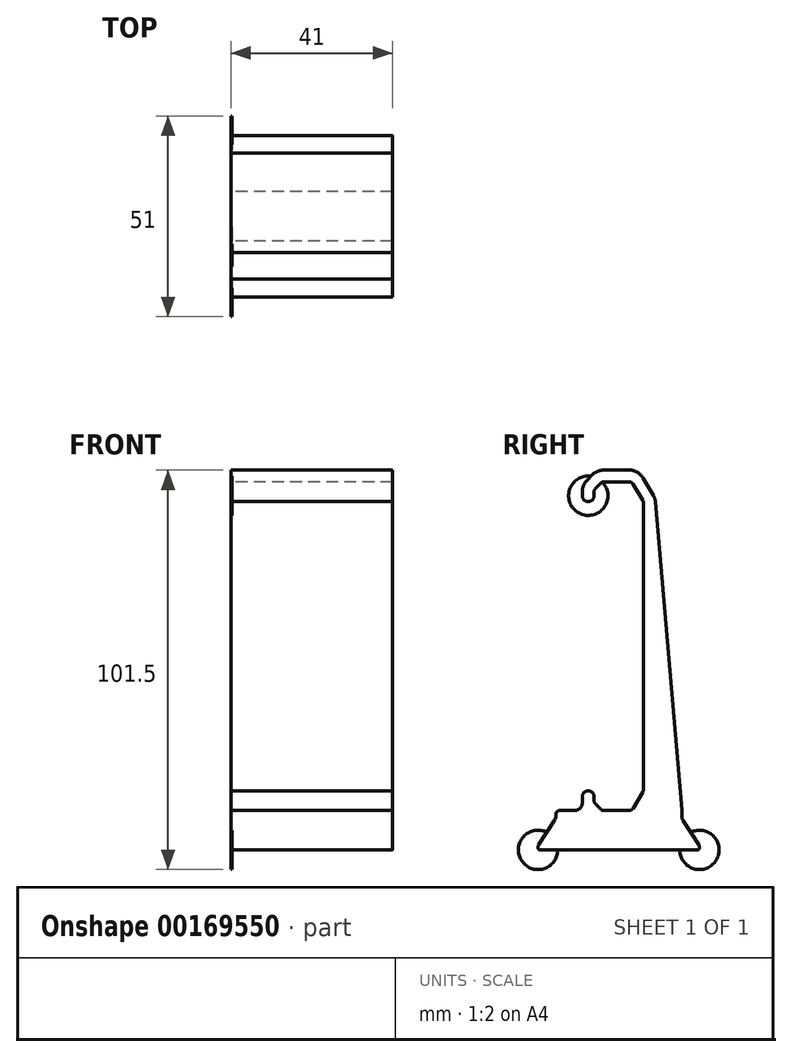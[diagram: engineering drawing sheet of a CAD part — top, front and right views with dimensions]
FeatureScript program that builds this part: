
annotation { "Feature Type Name" : "Feature", "Feature Type Description" : "" }
export const myFeature = defineFeature(function(context is Context, id is Id, definition is map)
    precondition{}
    {
        {
            var Q0;
            Q0=qCreatedBy(makeId("Right.planeOp"),FACE);
            var sketch = newSketch(context, id + "F0", { "sketchPlane" : qUnion([Q0])});
            skLineSegment(sketch, "E0", {"start": v(0, 0) * mm, "end": v(-20, 0) * mm});
            skLineSegment(sketch, "E1", {"start": v(-20.5, 0.5) * mm, "end": v(-20.5, 0.7) * mm});
            skLineSegment(sketch, "E2", {"start": v(-16, 8) * mm, "end": v(0, 8) * mm, "construction": true});
            skLineSegment(sketch, "E3", {"start": v(0, 8) * mm, "end": v(0, 0) * mm, "construction": true});
            skLineSegment(sketch, "E4", {"start": v(-16, 8.59) * mm, "end": v(-16, 9) * mm});
            skLineSegment(sketch, "E5", {"start": v(-3.84, 10) * mm, "end": v(0, 10) * mm});
            skLineSegment(sketch, "E6", {"start": v(0, 10) * mm, "end": v(0, 8) * mm, "construction": true});
            skLineSegment(sketch, "E7", {"start": v(-20.34, 1.25) * mm, "end": v(-16.32, 7.5) * mm});
            skLineSegment(sketch, "E8.MirrorCS", {"start": v(2.68, 10) * mm, "end": v(0, 10) * mm});
            skLineSegment(sketch, "E9.MirrorCS", {"start": v(16, 8.59) * mm, "end": v(16, 9.98) * mm});
            skLineSegment(sketch, "E10.MirrorCS", {"start": v(16, 8) * mm, "end": v(0, 8) * mm, "construction": true});
            skLineSegment(sketch, "E11.MirrorCS", {"start": v(20.34, 1.25) * mm, "end": v(16.32, 7.5) * mm});
            skLineSegment(sketch, "E12.MirrorCS", {"start": v(20.5, 0.5) * mm, "end": v(20.5, 0.7) * mm});
            skLineSegment(sketch, "E13.MirrorCS", {"start": v(0, 0) * mm, "end": v(20, 0) * mm});
            skLineSegment(sketch, "E14", {"start": v(6.25, 15.28) * mm, "end": v(6.25, 88.22) * mm});
            skLineSegment(sketch, "E15", {"start": v(2.68, 93.5) * mm, "end": v(-3.84, 93.5) * mm});
            skLineSegment(sketch, "E16", {"start": v(-6.25, 91.09) * mm, "end": v(-6.25, 90) * mm});
            skLineSegment(sketch, "E17", {"start": v(3.54, 10.49) * mm, "end": v(6.1, 14.76) * mm});
            skLineSegment(sketch, "E18", {"start": v(-4.54, 10.3) * mm, "end": v(-5.96, 11.7) * mm});
            skLineSegment(sketch, "E19", {"start": v(-4.54, 93.2) * mm, "end": v(-5.96, 91.8) * mm});
            skLineSegment(sketch, "E20", {"start": v(3.54, 93.01) * mm, "end": v(6.1, 88.74) * mm});
            skPoint(sketch, "E21.orphan", {"position": v(-6.25, 93.5) * mm});
            skPoint(sketch, "E22.orphan", {"position": v(6.25, 93.5) * mm});
            skPoint(sketch, "E23.orphan", {"position": v(-6.25, 10) * mm});
            skPoint(sketch, "E24.orphan", {"position": v(6.25, 10) * mm});
            skLineSegment(sketch, "E25", {"start": v(-6.25, 10) * mm, "end": v(-6.25, 12) * mm, "construction": true});
            skLineSegment(sketch, "E26", {"start": v(6.25, 10) * mm, "end": v(6.25, 15) * mm, "construction": true});
            skLineSegment(sketch, "E27", {"start": v(-6.25, 93.5) * mm, "end": v(-4.25, 93.5) * mm, "construction": true});
            skLineSegment(sketch, "E28", {"start": v(-6.25, 93.5) * mm, "end": v(-6.25, 91.5) * mm, "construction": true});
            skLineSegment(sketch, "E29", {"start": v(3.25, 93.5) * mm, "end": v(6.25, 93.5) * mm, "construction": true});
            skLineSegment(sketch, "E30", {"start": v(6.25, 93.5) * mm, "end": v(6.25, 88.5) * mm, "construction": true});
            skPoint(sketch, "E31.visualSharp", {"position": v(-6.25, 91.5) * mm});
            skArc(sketch, "E31.filletArc", {"start": v(-5.96, 91.8) * mm, "mid": v(-6.17, 91.47) * mm, "end": v(-6.25, 91.09) * mm});
            skPoint(sketch, "E32.visualSharp", {"position": v(-4.25, 93.5) * mm});
            skArc(sketch, "E32.filletArc", {"start": v(-3.84, 93.5) * mm, "mid": v(-4.22, 93.42) * mm, "end": v(-4.54, 93.2) * mm});
            skPoint(sketch, "E33.visualSharp", {"position": v(3.25, 93.5) * mm});
            skArc(sketch, "E33.filletArc", {"start": v(3.54, 93.01) * mm, "mid": v(3.18, 93.37) * mm, "end": v(2.68, 93.5) * mm});
            skPoint(sketch, "E34.visualSharp", {"position": v(6.25, 88.5) * mm});
            skArc(sketch, "E34.filletArc", {"start": v(6.25, 88.22) * mm, "mid": v(6.21, 88.49) * mm, "end": v(6.1, 88.74) * mm});
            skPoint(sketch, "E35.visualSharp", {"position": v(6.25, 15) * mm});
            skArc(sketch, "E35.filletArc", {"start": v(6.1, 14.76) * mm, "mid": v(6.21, 15.01) * mm, "end": v(6.25, 15.28) * mm});
            skPoint(sketch, "E36.newPointA", {"position": v(3.25, 10) * mm});
            skPoint(sketch, "E36.newPointB", {"position": v(16, 10) * mm});
            skArc(sketch, "E36.filletArc", {"start": v(2.68, 10) * mm, "mid": v(3.18, 10.13) * mm, "end": v(3.54, 10.49) * mm});
            skPoint(sketch, "E37.newPointA", {"position": v(-16, 10) * mm});
            skPoint(sketch, "E37.newPointB", {"position": v(-4.25, 10) * mm});
            skArc(sketch, "E37.filletArc", {"start": v(-4.54, 10.3) * mm, "mid": v(-4.22, 10.08) * mm, "end": v(-3.84, 10) * mm});
            skPoint(sketch, "E38.visualSharp", {"position": v(-6.25, 12) * mm});
            skArc(sketch, "E38.filletArc", {"start": v(-6.25, 12.41) * mm, "mid": v(-6.17, 12.03) * mm, "end": v(-5.96, 11.7) * mm});
            skLineSegment(sketch, "E39", {"start": v(-7.75, 15) * mm, "end": v(-7.75, 15) * mm});
            skLineSegment(sketch, "E40", {"start": v(-9.25, 13.5) * mm, "end": v(-9.25, 12) * mm});
            skLineSegment(sketch, "E41", {"start": v(-11.25, 10) * mm, "end": v(-15, 10) * mm});
            skLineSegment(sketch, "E42", {"start": v(2.68, 96.5) * mm, "end": v(-3.84, 96.5) * mm});
            skLineSegment(sketch, "E43", {"start": v(-9.25, 91.09) * mm, "end": v(-9.25, 90) * mm});
            skLineSegment(sketch, "E44", {"start": v(-7.75, 88.5) * mm, "end": v(-7.75, 88.5) * mm});
            skLineSegment(sketch, "E45", {"start": v(-8.08, 93.91) * mm, "end": v(-6.66, 95.33) * mm});
            skLineSegment(sketch, "E46", {"start": v(8.78, 90.12) * mm, "end": v(6.11, 94.56) * mm});
            skPoint(sketch, "E47.orphan", {"position": v(-9.25, 96.5) * mm});
            skLineSegment(sketch, "E48", {"start": v(-9.25, 92.74) * mm, "end": v(-9.25, 96.5) * mm, "construction": true});
            skLineSegment(sketch, "E49", {"start": v(-9.25, 96.5) * mm, "end": v(-5.5, 96.5) * mm, "construction": true});
            skLineSegment(sketch, "E50", {"start": v(9.25, 89.33) * mm, "end": v(9.25, 96.5) * mm, "construction": true});
            skLineSegment(sketch, "E51", {"start": v(9.25, 96.5) * mm, "end": v(4.95, 96.5) * mm, "construction": true});
            skPoint(sketch, "E52.visualSharp", {"position": v(-9.25, 92.74) * mm});
            skArc(sketch, "E52.filletArc", {"start": v(-8.08, 93.91) * mm, "mid": v(-8.95, 92.62) * mm, "end": v(-9.25, 91.09) * mm});
            skPoint(sketch, "E53.visualSharp", {"position": v(-5.5, 96.5) * mm});
            skArc(sketch, "E53.filletArc", {"start": v(-3.84, 96.5) * mm, "mid": v(-5.37, 96.2) * mm, "end": v(-6.66, 95.33) * mm});
            skPoint(sketch, "E54.visualSharp", {"position": v(4.95, 96.5) * mm});
            skArc(sketch, "E54.filletArc", {"start": v(6.11, 94.56) * mm, "mid": v(4.65, 95.98) * mm, "end": v(2.68, 96.5) * mm});
            skPoint(sketch, "E55.visualSharp", {"position": v(9.25, 89.33) * mm});
            skArc(sketch, "E55.filletArc", {"start": v(9.24, 89.46) * mm, "mid": v(9.2, 89.47) * mm, "end": v(9.2, 89.43) * mm});
            skPoint(sketch, "E56.visualSharp", {"position": v(-9.25, 88.5) * mm});
            skArc(sketch, "E56.filletArc", {"start": v(-9.25, 90) * mm, "mid": v(-8.81, 88.94) * mm, "end": v(-7.75, 88.5) * mm});
            skPoint(sketch, "E57.newPointA", {"position": v(-6.25, 88.5) * mm});
            skArc(sketch, "E57.filletArc", {"start": v(-7.75, 88.5) * mm, "mid": v(-6.69, 88.94) * mm, "end": v(-6.25, 90) * mm});
            skLineSegment(sketch, "E58", {"start": v(-6.25, 13.5) * mm, "end": v(-6.25, 12.41) * mm});
            skPoint(sketch, "E59.visualSharp", {"position": v(-6.25, 15) * mm});
            skArc(sketch, "E59.filletArc", {"start": v(-6.25, 13.5) * mm, "mid": v(-6.69, 14.56) * mm, "end": v(-7.75, 15) * mm});
            skPoint(sketch, "E60.visualSharp", {"position": v(-9.25, 15) * mm});
            skArc(sketch, "E60.filletArc", {"start": v(-7.75, 15) * mm, "mid": v(-8.81, 14.56) * mm, "end": v(-9.25, 13.5) * mm});
            skPoint(sketch, "E61.visualSharp", {"position": v(-20.5, 1) * mm});
            skArc(sketch, "E61.filletArc", {"start": v(-20.34, 1.25) * mm, "mid": v(-20.46, 0.99) * mm, "end": v(-20.5, 0.7) * mm});
            skPoint(sketch, "E62.visualSharp", {"position": v(-16, 8) * mm});
            skArc(sketch, "E62.filletArc", {"start": v(-16.32, 7.5) * mm, "mid": v(-16.08, 8.02) * mm, "end": v(-16, 8.59) * mm});
            skArc(sketch, "E63.filletArc", {"start": v(-15, 10) * mm, "mid": v(-15.7, 9.7) * mm, "end": v(-16, 9) * mm});
            skPoint(sketch, "E64.visualSharp", {"position": v(-9.25, 10) * mm});
            skArc(sketch, "E64.filletArc", {"start": v(-11.25, 10) * mm, "mid": v(-9.84, 10.59) * mm, "end": v(-9.25, 12) * mm});
            skPoint(sketch, "E65.visualSharp", {"position": v(9.25, 10) * mm});
            skLineSegment(sketch, "E66.filletArc", {"start": v(16, 10.06) * mm, "end": v(16, 10.06) * mm});
            skPoint(sketch, "E67.visualSharp", {"position": v(16, 8) * mm});
            skArc(sketch, "E67.filletArc", {"start": v(16, 8.59) * mm, "mid": v(16.08, 8.02) * mm, "end": v(16.32, 7.5) * mm});
            skPoint(sketch, "E68.visualSharp", {"position": v(20.5, 1) * mm});
            skArc(sketch, "E68.filletArc", {"start": v(20.5, 0.7) * mm, "mid": v(20.46, 0.99) * mm, "end": v(20.34, 1.25) * mm});
            skPoint(sketch, "E69.visualSharp", {"position": v(20.5, 0) * mm});
            skArc(sketch, "E69.filletArc", {"start": v(20, 0) * mm, "mid": v(20.35, 0.15) * mm, "end": v(20.5, 0.5) * mm});
            skPoint(sketch, "E70.visualSharp", {"position": v(-20.5, 0) * mm});
            skArc(sketch, "E70.filletArc", {"start": v(-20.5, 0.5) * mm, "mid": v(-20.35, 0.15) * mm, "end": v(-20, 0) * mm});
            skLineSegment(sketch, "E71", {"start": v(16, 10.15) * mm, "end": v(9.33, 88.4) * mm});
            skArc(sketch, "E72.filletArc", {"start": v(16, 9.98) * mm, "mid": v(16, 10.06) * mm, "end": v(16, 10.15) * mm});
            skArc(sketch, "E73.filletArc", {"start": v(9.33, 88.4) * mm, "mid": v(9.16, 89.29) * mm, "end": v(8.78, 90.12) * mm});
            skLineSegment(sketch, "E74", {"start": v(-7.75, 88.5) * mm, "end": v(-7.75, 90) * mm, "construction": true});
            skLineSegment(sketch, "E75", {"start": v(0, 0) * mm, "end": v(0, 96.5) * mm, "construction": true});
            skLineSegment(sketch, "E76", {"start": v(-7.75, 90) * mm, "end": v(0, 90) * mm, "construction": true});
            skSolve(sketch);
        }
        {
            var Q0;
            Q0 = qSketchRegion(id + "F0", true);
            extrude(context, id + "F1", {"entities" : qUnion([Q0]), "depth" : 41 * mm});
        }
        {
            var Q0;
            Q0=qCreatedBy(makeId("Right.planeOp"),FACE);
            var sketch = newSketch(context, id + "F2", { "sketchPlane" : qUnion([Q0])});
            skCircle(sketch, "E77", {"center": v(-20.5, 0) * mm, "radius": 5 * mm});
            skCircle(sketch, "E78", {"center": v(20.5, 0) * mm, "radius": 5 * mm});
            skCircle(sketch, "E79", {"center": v(-7.75, 90) * mm, "radius": 5 * mm});
            skSolve(sketch);
        }
        {
            var Q0;
            Q0 = qSketchRegion(id + "F2", true);
            extrude(context, id + "F3", {"entities" : qUnion([Q0]), "operationType" : NewBodyOperationType.ADD, "depth" : 0.3 * mm});
        }
    });
